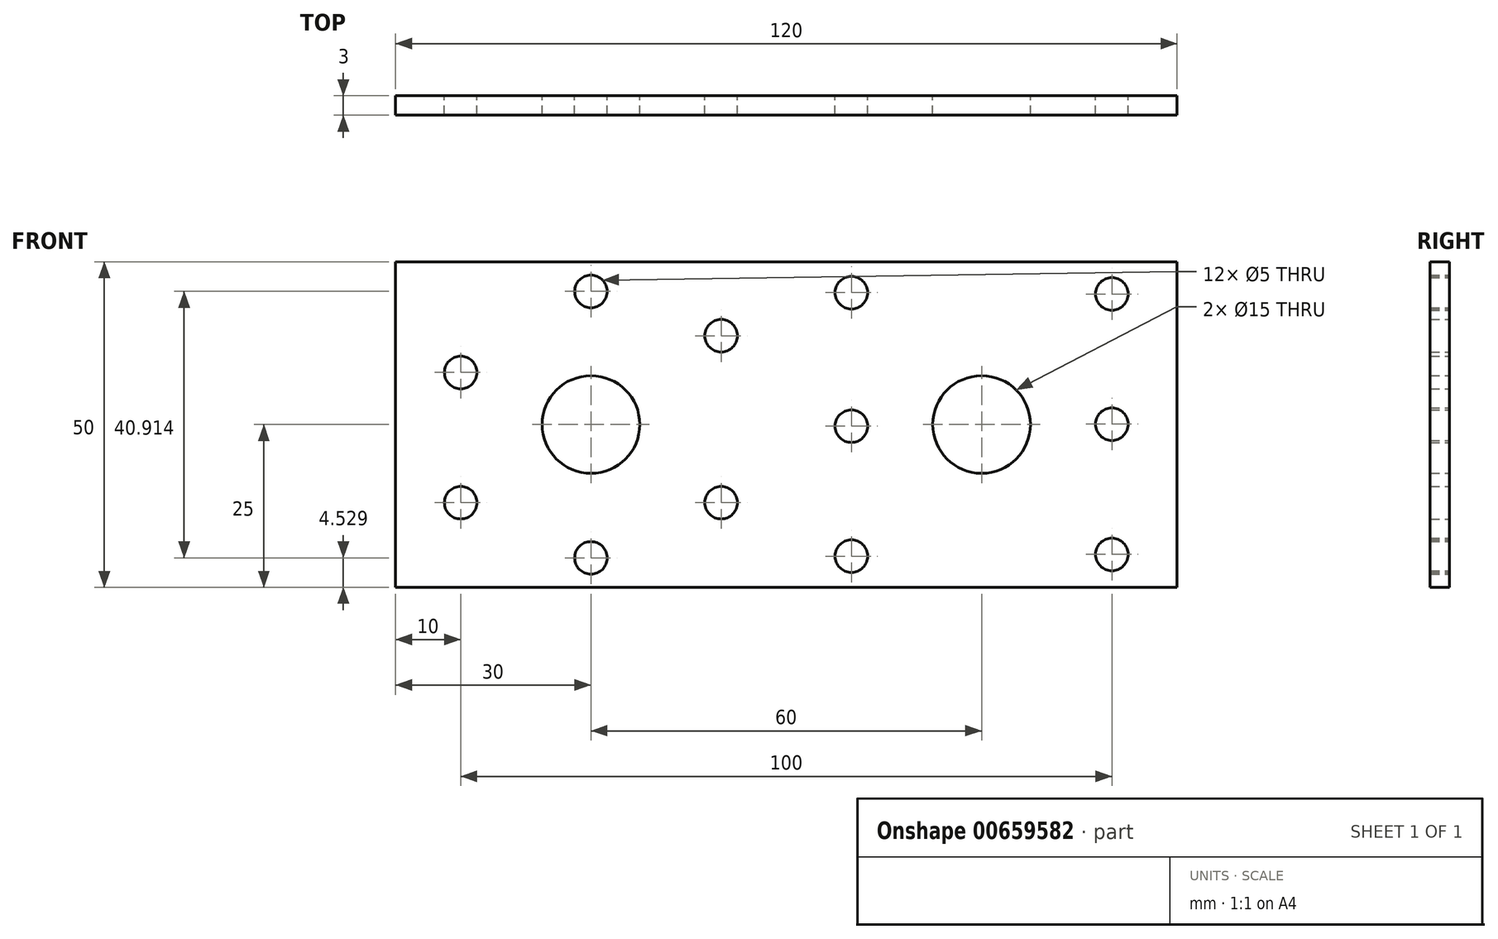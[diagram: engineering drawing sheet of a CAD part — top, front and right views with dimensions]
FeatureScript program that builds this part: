
annotation { "Feature Type Name" : "Feature", "Feature Type Description" : "" }
export const myFeature = defineFeature(function(context is Context, id is Id, definition is map)
    precondition{}
    {
        {
            var Q0;
            Q0=qCreatedBy(makeId("Front.planeOp"),FACE);
            var sketch = newSketch(context, id + "F0", { "sketchPlane" : qUnion([Q0])});
            skLineSegment(sketch, "E0.bottom", {"start": v(-60, -25) * mm, "end": v(60, -25) * mm});
            skLineSegment(sketch, "E0.top", {"start": v(-60, 25) * mm, "end": v(60, 25) * mm});
            skLineSegment(sketch, "E0.left", {"start": v(-60, -25) * mm, "end": v(-60, 25) * mm});
            skLineSegment(sketch, "E0.right", {"start": v(60, -25) * mm, "end": v(60, 25) * mm});
            skPoint(sketch, "E0.middle", {"position": v(0, 0) * mm});
            skCircle(sketch, "E1", {"center": v(50, 20.06) * mm, "radius": 2.5 * mm});
            skCircle(sketch, "E2.1.0.0", {"center": v(50, 0.06) * mm, "radius": 2.5 * mm});
            skCircle(sketch, "E2.2.0.0", {"center": v(50, -19.94) * mm, "radius": 2.5 * mm});
            skCircle(sketch, "E3", {"center": v(30, 0) * mm, "radius": 7.5 * mm});
            skCircle(sketch, "E4.1.0.0", {"center": v(-30, 0) * mm, "radius": 7.5 * mm});
            skCircle(sketch, "E5.1.0.0", {"center": v(10, 20.25) * mm, "radius": 2.5 * mm});
            skCircle(sketch, "E5.2.0.0", {"center": v(-30, 20.44) * mm, "radius": 2.5 * mm});
            skCircle(sketch, "E6.1.0.0", {"center": v(10, -20.2) * mm, "radius": 2.5 * mm});
            skCircle(sketch, "E6.2.0.0", {"center": v(-30, -20.47) * mm, "radius": 2.5 * mm});
            skCircle(sketch, "E7.1.0.0", {"center": v(10, -0.25) * mm, "radius": 2.5 * mm});
            skCircle(sketch, "E8", {"center": v(-50, 8) * mm, "radius": 2.5 * mm});
            skCircle(sketch, "E9.1.0.0", {"center": v(-10, 13.64) * mm, "radius": 2.5 * mm});
            skCircle(sketch, "E10.1.0.0", {"center": v(-50, -12) * mm, "radius": 2.5 * mm});
            skCircle(sketch, "E11.1.0.0", {"center": v(-10, -12) * mm, "radius": 2.5 * mm});
            skSolve(sketch);
        }
        {
            var Q0;
            Q0 = qSketchRegion(id + "F0", true);
            extrude(context, id + "F1", {"entities" : qUnion([Q0]), "depth" : 3 * mm, "offsetDistance" : 25 * mm});
        }
    });
